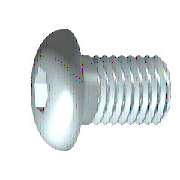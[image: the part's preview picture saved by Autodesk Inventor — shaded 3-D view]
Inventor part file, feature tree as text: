
AUTODESK INVENTOR PART (.ipt)
format: ipt  version: 2023.4 (Build 274418000, 418)  size: 194,048 bytes
history: native  units: mm (DEFAULTED — no unit token found)
features: extrude x1, plane x1, fillet x1
ambient origin geometry x7: Origin, YZ Plane, XY Plane, X Axis, Y Axis, Z Axis, Center Point
bodies: Solid1 (feature_tree), Body (feature_tree)
feature tree (3):
  extrude  "Slot"  Depth=10.5916mm
  plane  "Work Plane1"
  fillet  "Fillet2"  Radius=2.1083mm
